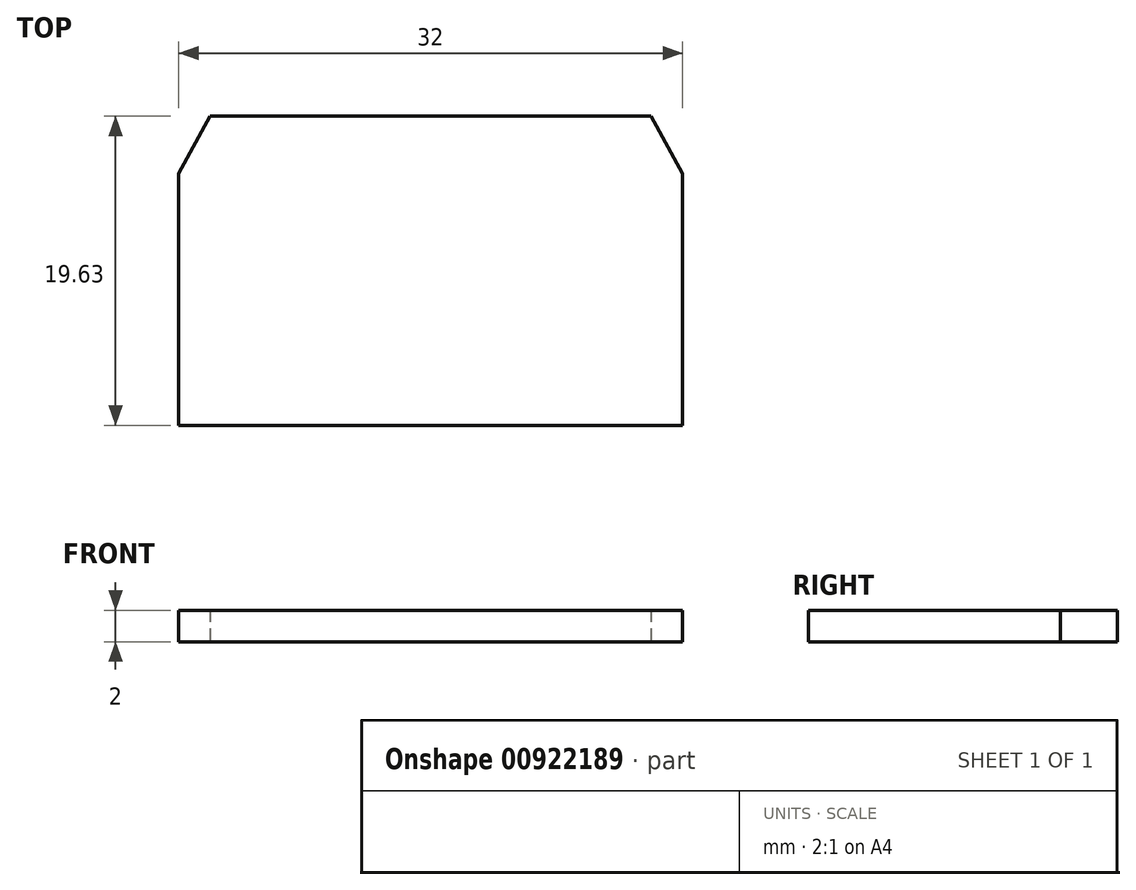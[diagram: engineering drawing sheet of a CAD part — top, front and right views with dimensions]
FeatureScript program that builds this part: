
annotation { "Feature Type Name" : "Feature", "Feature Type Description" : "" }
export const myFeature = defineFeature(function(context is Context, id is Id, definition is map)
    precondition{}
    {
        {
            var Q0;
            Q0=qCreatedBy(makeId("Top.planeOp"),FACE);
            var sketch = newSketch(context, id + "F0", { "sketchPlane" : qUnion([Q0])});
            skLineSegment(sketch, "E0.bottom", {"start": v(-16, -8) * mm, "end": v(16, -8) * mm});
            skLineSegment(sketch, "E0.left", {"start": v(-16, -8) * mm, "end": v(-16, 8) * mm});
            skLineSegment(sketch, "E0.right", {"start": v(16, -8) * mm, "end": v(16, 8) * mm});
            skLineSegment(sketch, "E1", {"start": v(-16, 8) * mm, "end": v(-14, 11.63) * mm});
            skLineSegment(sketch, "E2", {"start": v(-14, 11.63) * mm, "end": v(14, 11.63) * mm});
            skLineSegment(sketch, "E3", {"start": v(14, 11.63) * mm, "end": v(16, 8) * mm});
            skSolve(sketch);
        }
        {
            var Q0;
            Q0=makeQuery(id+"F0.imprint","IMPRINT",FACE,{"disambiguationData":[TD([[makeQuery(id+"F0.imprint","IMPRINT",EDGE,{"derivedFrom":sQuery(id+"F0.wireOp",EDGE,"E0.bottom")}),1.0]])]});
            extrude(context, id + "F1", {"entities" : qUnion([Q0]), "depth" : 2 * mm, "offsetDistance" : 25 * mm});
        }
    });
